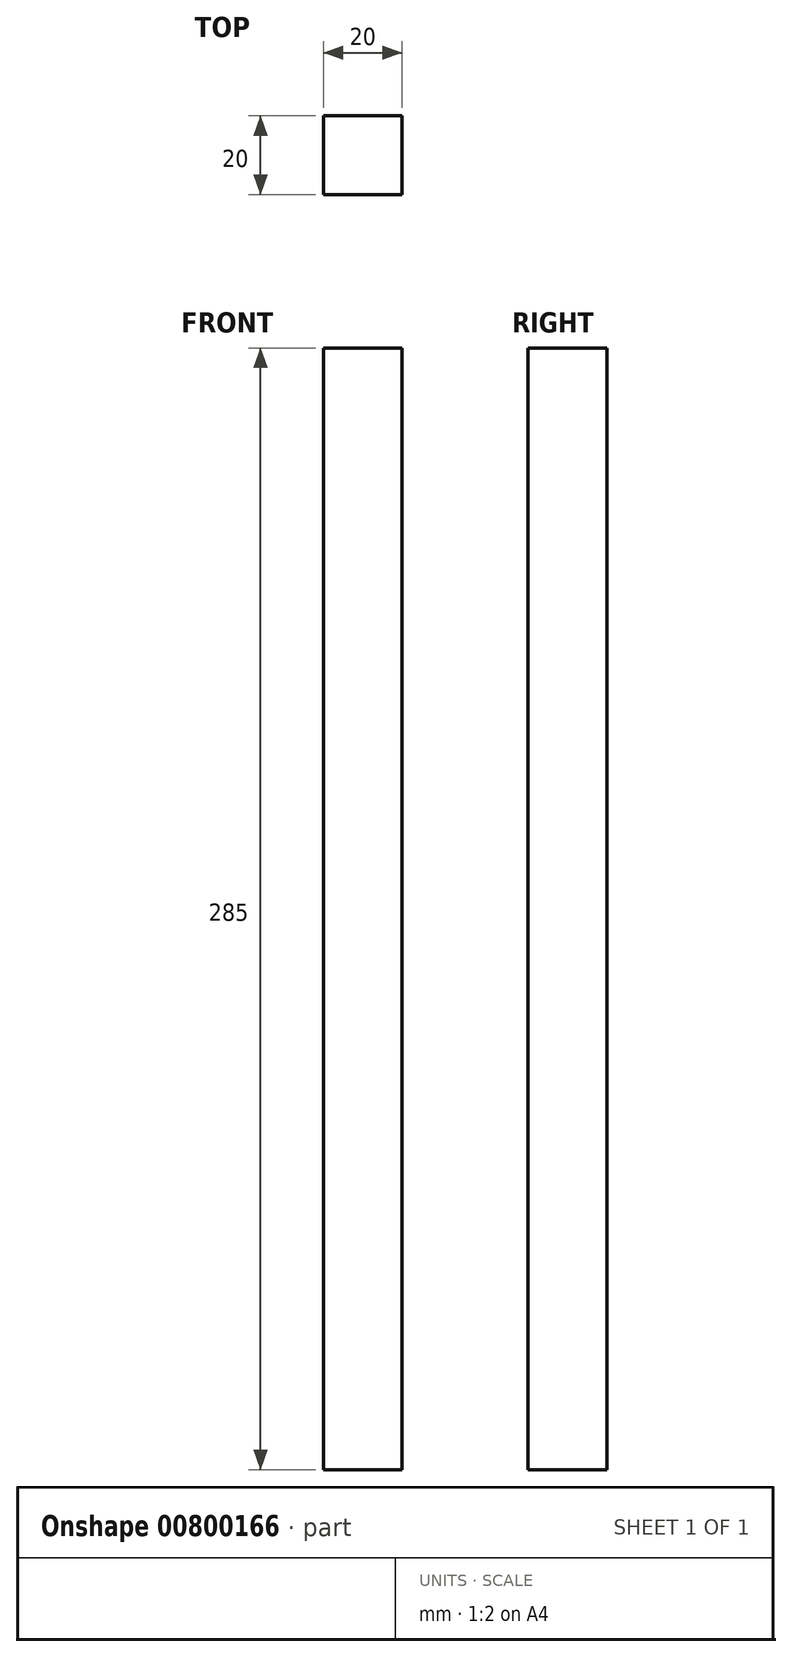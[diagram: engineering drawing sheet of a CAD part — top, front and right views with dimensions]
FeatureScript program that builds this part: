
annotation { "Feature Type Name" : "Feature", "Feature Type Description" : "" }
export const myFeature = defineFeature(function(context is Context, id is Id, definition is map)
    precondition{}
    {
        {
            var Q0;
            Q0=qCreatedBy(makeId("Top.planeOp"),FACE);
            var sketch = newSketch(context, id + "F0", { "sketchPlane" : qUnion([Q0])});
            skLineSegment(sketch, "E0.bottom", {"start": v(10, -10) * mm, "end": v(-10, -10) * mm});
            skLineSegment(sketch, "E0.top", {"start": v(10, 10) * mm, "end": v(-10, 10) * mm});
            skLineSegment(sketch, "E0.left", {"start": v(10, -10) * mm, "end": v(10, 10) * mm});
            skLineSegment(sketch, "E0.right", {"start": v(-10, -10) * mm, "end": v(-10, 10) * mm});
            skPoint(sketch, "E0.middle", {"position": v(0, 0) * mm});
            skSolve(sketch);
        }
        {
            var Q0;
            Q0=makeQuery(id+"F0.imprint","IMPRINT",FACE,{"disambiguationData":[TD([[makeQuery(id+"F0.imprint","IMPRINT",EDGE,{"derivedFrom":sQuery(id+"F0.wireOp",EDGE,"E0.bottom")}),-1.0]])]});
            extrude(context, id + "F1", {"entities" : qUnion([Q0]), "depth" : 285 * mm, "offsetDistance" : 25 * mm});
        }
    });
